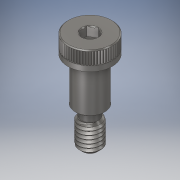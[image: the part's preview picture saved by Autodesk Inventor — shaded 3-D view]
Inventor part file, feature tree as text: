
AUTODESK INVENTOR PART (.ipt)
format: ipt  version: 2017 (Build 210142000, 142)  size: 602,112 bytes
history: native  units: in
note: dims shown in document units (in); Inventor stores cm internally (conversion verified against a paired STEP export)
features: chamfer x1
ambient origin geometry x8: Origin, YZ Plane, XZ Plane, XY Plane, X Axis, Y Axis, Z Axis, Center Point
bodies: Solid1 (feature_tree)
feature tree (1):
  chamfer  "Chamfer3"  [1 undecoded]
note: 1 required parameter value undecoded (feature->parameter linkage not recoverable at this tier; creation-order binding heuristic only, values carry confidence <= 0.55)
